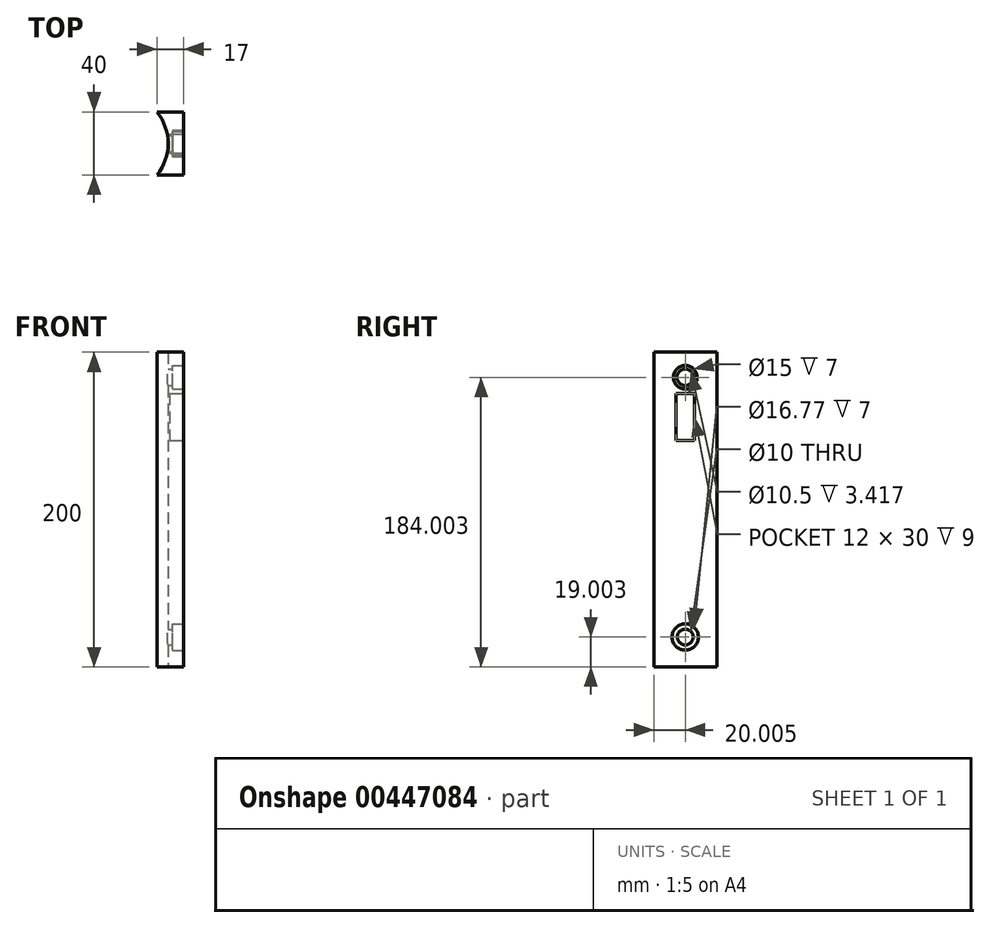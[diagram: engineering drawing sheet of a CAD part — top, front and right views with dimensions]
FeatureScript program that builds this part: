
annotation { "Feature Type Name" : "Feature", "Feature Type Description" : "" }
export const myFeature = defineFeature(function(context is Context, id is Id, definition is map)
    precondition{}
    {
        {
            var Q0;
            Q0=qCreatedBy(makeId("Right.planeOp"),FACE);
            var sketch = newSketch(context, id + "F0", { "sketchPlane" : qUnion([Q0])});
            skLineSegment(sketch, "E0.bottom", {"start": v(-0.44, 153.83) * mm, "end": v(39.56, 153.83) * mm});
            skLineSegment(sketch, "E0.top", {"start": v(-0.44, -46.17) * mm, "end": v(39.56, -46.17) * mm});
            skLineSegment(sketch, "E0.left", {"start": v(-0.44, 153.83) * mm, "end": v(-0.44, -46.17) * mm});
            skLineSegment(sketch, "E0.right", {"start": v(39.56, 153.83) * mm, "end": v(39.56, -46.17) * mm});
            skSolve(sketch);
        }
        {
            var Q0;
            Q0 = qSketchRegion(id + "F0", true);
            extrude(context, id + "F1", {"entities" : qUnion([Q0]), "depth" : 17 * mm, "offsetDistance" : 25 * mm});
        }
        {
            var Q0;
            Q0=qCreatedBy(makeId("Top.planeOp"),FACE);
            var sketch = newSketch(context, id + "F2", { "sketchPlane" : qUnion([Q0])});
            skCircle(sketch, "E1", {"center": v(-24.98, 19.56) * mm, "radius": 32 * mm});
            skSolve(sketch);
        }
        {
            var Q0;
            Q0=makeQuery(id+"F2.imprint","IMPRINT",FACE,{"disambiguationData":[TD([[makeQuery(id+"F2.imprint","IMPRINT",EDGE,{"derivedFrom":sQuery(id+"F2.wireOp",EDGE,"E1")}),1.0]])]});
            extrude(context, id + "F3", {"entities" : qUnion([Q0]), "operationType" : NewBodyOperationType.REMOVE, "endBound" : BoundingType.SYMMETRIC, "depth" : 374 * mm, "offsetDistance" : 25 * mm});
        }
        {
            var Q0;
            Q0 = qSketchRegion(id + "F2", true);
            extrude(context, id + "F4", {"entities" : qUnion([Q0]), "operationType" : NewBodyOperationType.REMOVE, "oppositeDirection" : true, "depth" : 195 * mm, "offsetDistance" : 25 * mm});
        }
        {
            var Q0;
            Q0=makeQuery(id+"F1.opExtrude","CAP_FACE",FACE,{"disambiguationData":[OSD([sQuery(id+"F0.wireOp",EDGE,"E0.bottom"),sQuery(id+"F0.wireOp",EDGE,"E0.top"),sQuery(id+"F0.wireOp",EDGE,"E0.left"),sQuery(id+"F0.wireOp",EDGE,"E0.right")])],"isStart":false});
            var sketch = newSketch(context, id + "F5", { "sketchPlane" : qUnion([Q0])});
            skCircle(sketch, "E2", {"center": v(19.56, -27.17) * mm, "radius": 8.38 * mm});
            skCircle(sketch, "E3", {"center": v(19.56, 137.83) * mm, "radius": 7.5 * mm});
            skSolve(sketch);
        }
        {
            var Q0;
            Q0 = qSketchRegion(id + "F5", true);
            extrude(context, id + "F6", {"entities" : qUnion([Q0]), "operationType" : NewBodyOperationType.REMOVE, "oppositeDirection" : true, "depth" : 7 * mm, "offsetDistance" : 25 * mm});
        }
        {
            var Q0;
            Q0=makeQuery(id+"F6.boolean.opBoolean","COPY",FACE,{"derivedFrom":makeQuery(id+"F6.opExtrude","CAP_FACE",FACE,{"disambiguationData":[OSD([sQuery(id+"F5.wireOp",EDGE,"E2")])],"isStart":false})});
            var sketch = newSketch(context, id + "F7", { "sketchPlane" : qUnion([Q0])});
            skCircle(sketch, "E4", {"center": v(19.56, -27.17) * mm, "radius": 5 * mm});
            skCircle(sketch, "E5", {"center": v(19.56, 137.83) * mm, "radius": 5.25 * mm});
            skSolve(sketch);
        }
        {
            var Q0;
            Q0 = qSketchRegion(id + "F7", true);
            extrude(context, id + "F8", {"entities" : qUnion([Q0]), "operationType" : NewBodyOperationType.REMOVE, "oppositeDirection" : true, "depth" : 25 * mm, "offsetDistance" : 25 * mm});
        }
        {
            var Q0;
            Q0=makeQuery(id+"F1.opExtrude","CAP_FACE",FACE,{"disambiguationData":[OSD([sQuery(id+"F0.wireOp",EDGE,"E0.bottom"),sQuery(id+"F0.wireOp",EDGE,"E0.top"),sQuery(id+"F0.wireOp",EDGE,"E0.left"),sQuery(id+"F0.wireOp",EDGE,"E0.right")])],"isStart":false});
            var sketch = newSketch(context, id + "F9", { "sketchPlane" : qUnion([Q0])});
            skLineSegment(sketch, "E6.bottom", {"start": v(13.56, 127.58) * mm, "end": v(25.56, 127.58) * mm});
            skLineSegment(sketch, "E6.top", {"start": v(13.56, 97.58) * mm, "end": v(25.56, 97.58) * mm});
            skLineSegment(sketch, "E6.left", {"start": v(13.56, 127.58) * mm, "end": v(13.56, 97.58) * mm});
            skLineSegment(sketch, "E6.right", {"start": v(25.56, 127.58) * mm, "end": v(25.56, 97.58) * mm});
            skSolve(sketch);
        }
        {
            var Q0;
            Q0 = qSketchRegion(id + "F9", true);
            extrude(context, id + "F10", {"entities" : qUnion([Q0]), "operationType" : NewBodyOperationType.REMOVE, "oppositeDirection" : true, "depth" : 9 * mm, "offsetDistance" : 25 * mm});
        }
    });
